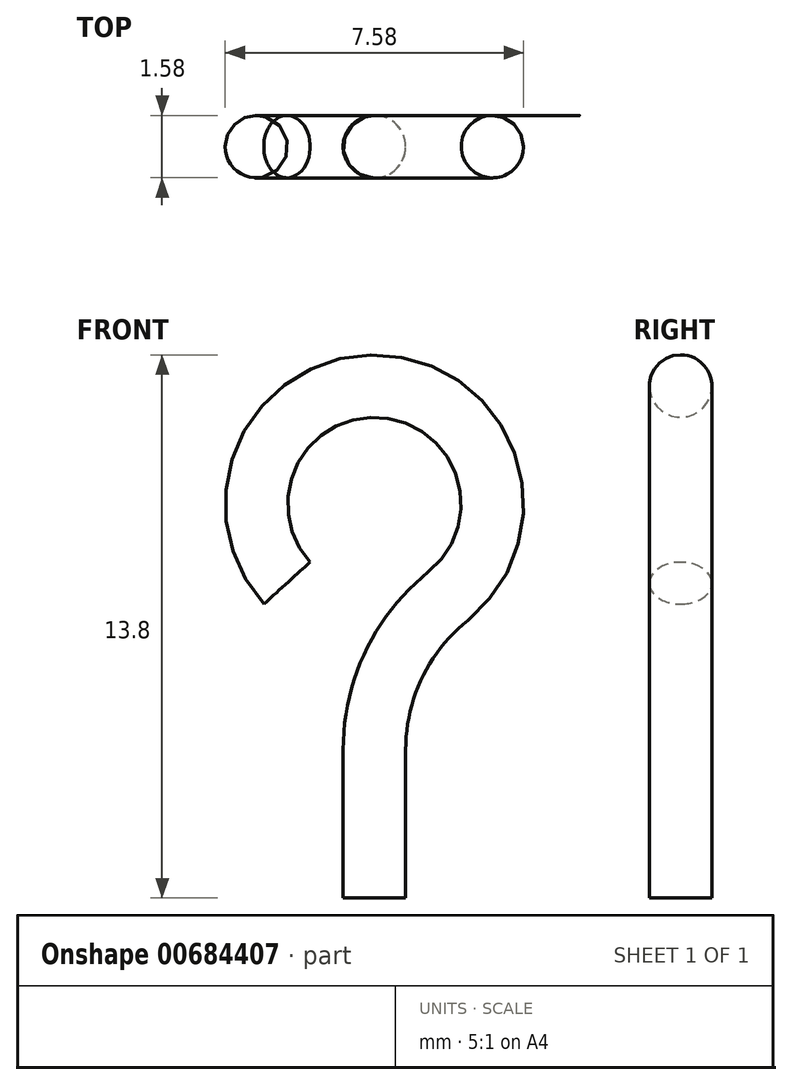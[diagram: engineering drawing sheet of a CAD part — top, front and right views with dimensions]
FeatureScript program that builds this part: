
annotation { "Feature Type Name" : "Feature", "Feature Type Description" : "" }
export const myFeature = defineFeature(function(context is Context, id is Id, definition is map)
    precondition{}
    {
        {
            var Q0;
            Q0=qCreatedBy(makeId("Front.planeOp"),FACE);
            var sketch = newSketch(context, id + "F0", { "sketchPlane" : qUnion([Q0])});
            skArc(sketch, "E0", {"start": v(1.87, -2.34) * mm, "mid": v(0.24, 2.99) * mm, "end": v(-2.22, -2.01) * mm});
            skLineSegment(sketch, "E1", {"start": v(0, 0) * mm, "end": v(-2.22, -2.01) * mm});
            skLineSegment(sketch, "E2", {"start": v(0, -6.24) * mm, "end": v(0, -10) * mm});
            skPoint(sketch, "E3.newPointB", {"position": v(0, -3) * mm});
            skArc(sketch, "E3.filletArc", {"start": v(1.87, -2.34) * mm, "mid": v(0.5, -4.08) * mm, "end": v(0, -6.24) * mm});
            skSolve(sketch);
        }
        {
            var Q0;
            Q0=qCreatedBy(makeId("Top.planeOp"),FACE);
            cPlane(context, id + "F1", {"entities" : qUnion([Q0]), "cplaneType" : CPlaneType.OFFSET, "offset" : 10 * mm, "oppositeDirection" : true, "width" : 152.4 * mm, "height" : 152.4 * mm});
        }
        {
            var Q0;
            Q0=qCreatedBy(id+"F1.planeOp",FACE);
            var sketch = newSketch(context, id + "F2", { "sketchPlane" : qUnion([Q0])});
            skCircle(sketch, "E4", {"center": v(0, 0) * mm, "radius": 0.8 * mm});
            skSolve(sketch);
        }
        {
            var Q0;
            Q0=makeQuery(id+"F2.imprint","IMPRINT",FACE,{"disambiguationData":[TD([[makeQuery(id+"F2.imprint","IMPRINT",EDGE,{"derivedFrom":sQuery(id+"F2.wireOp",EDGE,"E4")}),1.0]])]});
            var Q1;
            Q1=sQuery(id+"F0.wireOp",EDGE,"E2");
            var Q2;
            Q2=sQuery(id+"F0.wireOp",EDGE,"E3.filletArc");
            var Q3;
            Q3=sQuery(id+"F0.wireOp",EDGE,"E0");
            sweep(context, id + "F3", {"profiles" : qUnion([Q0]), "path" : qUnion([Q1, Q2, Q3])});
        }
    });
